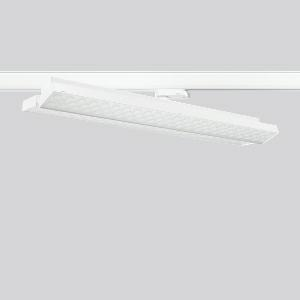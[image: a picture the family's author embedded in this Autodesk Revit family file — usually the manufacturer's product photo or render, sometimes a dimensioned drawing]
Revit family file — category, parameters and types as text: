
# Revit family: tx-move_742163_002_7894
name_source: partatom
category: Lighting Fixtures
units: mm (PartAtom-declared; Revit-internal decimal feet)

## family parameters
Cut with Voids When Loaded = No
Host = Face
Light Source = No
Part Type = Normal
Room Calculation Point = No
Round Connector Dimension = Use Diameter
Shared = No

## types (1)
- MultiLumen 1 (1 x LED Modul 830, 2750 lm, 3000)
    Apparent Load = 41 VA
    CIE Flux Codes = 65 90 98 100 100
    Color Rendering = 80
    Color Temperature = 3000
    Default Elevation = 1800 mm
    Description = Series: TX-MOVE
Multifunctional surface-mounted spotlight for area lighting. Very flat design. Housing: sheet steel, powder-coated. Rotation range: 356°. Swivel range: 90°. Consistent alignment possible with visible tilt scale. High-efficiency LED units with optimum light control thanks to clear plastic (PC) lens optics. Spezielle Mikrostrukturen reduzieren Gelbsaum. Asymmetrical light distribution. With multi adaptor for 3-circuit tracks 230 V. Suitable for Track on ceiling. MultiLumen: Luminous flux adjustable in 3 steps. Factory setting is the highest luminous flux. Environmentally friendly and resource-saving due to replaceable and recyclable components. 
Colour: traffic white, matt (RAL 9016)
Length: 570 mm
Width: 119 mm
Height: 92 mm
Lamp: LED
Socket: without socket
Colour temperature: 3000K
Colour rendering index (CRI): 80
System power: 41 W
Rated luminous flux: 5500 lm
Luminous efficiency: 134 lm/W
System power 2: 57 W
Rated luminous flux 2: 7400 lm
Luminous efficiency 2: 130 lm/W
System power 3: 73 W
Rated luminous flux 3: 9050 lm
Luminous efficiency 3: 124 lm/W
Control gear: Regulated power supply
Protection class: I
Type of protection: IP 20
    Height = 75 mm
    Lamp = 1 x LED Modul 830
    Lamp Light Flux = 2750 lm
    Lamp count = 1
    Length = 569 mm
    Lifetime = 50000 h
    Luminous efficacy = 134 lm/W
    Manufacturer = RZB
    ModVariant = No
    Model = 742163.002
    Mounting Place = Ceiling
    Mounting Type = Surface mounted
    Number of Poles = 1
    OnlyDefault = Yes
    Power Factor = 1
    Product Name = TX-MOVE
    Product group = Track mounted projectors
    ProductGroupID = 301
    Protection Class = Protection class I
    Protection Degree = IP 20
    RLX_Detail_Level = 1
    RLX_Emergency_Light_Flux = 0 lm
    RLX_Emergency_Type = 0
    RLX_Emergency_Type_DB = No
    RlxData = <blob elided: 51753 chars, md5=722f0701>
    Socket = socket
    Standby Power = 0 W
    System Light Flux = 5500 lm
    System Power = 41 W
    Type Comments = MultiLumen 1
    Type Image = 742162.002.jpg
    URL = http://relux.com
    VarID = multilumen_1
    Voltage = 0 V
    Weight = 0.00 kg
    Width = 119 mm

## geometry (parser evidence)
native form markers: Blend x4, Sweep x15
no freeform markers — native parametric forms only
